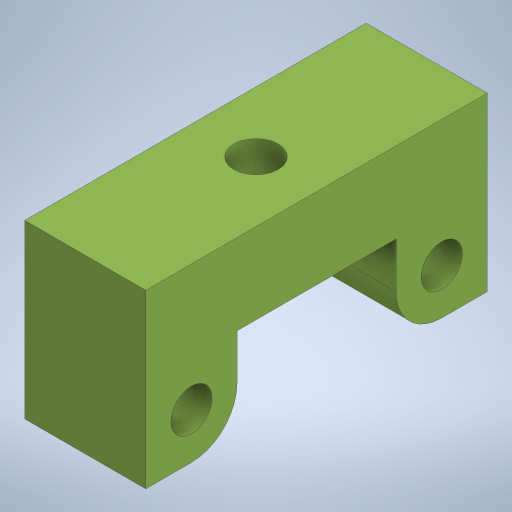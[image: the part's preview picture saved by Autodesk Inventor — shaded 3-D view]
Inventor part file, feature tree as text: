
AUTODESK INVENTOR PART (.ipt)
format: ipt  version: 2023.2 (Build 272271030, 271C)  size: 252,416 bytes
history: native  units: mm
features: extrude x3, sketch x2, plane x1, projected_geometry x1
ambient origin geometry x8: Origin, YZ Plane, XZ Plane, XY Plane, X Axis, Y Axis, Z Axis, Center Point
bodies: Body1 (feature_tree)
feature tree (7):
  sketch  "Sketch3"  dims[d19=11.3mm d20=5.65mm d23=10.0mm]
  plane  "Work Plane1"
  extrude  "Extrusion5"  Depth=10.0mm
  sketch  "Sketch5"  dims[d24=10.0mm d25=11.3mm d26=5.1mm d29=5.5mm d36=21.15mm d37=15.0mm d38=0.0mm d40=8.1mm d41=5.5mm d42=0.0mm d43=0.0mm d44=3.1mm d45=0.0mm d3=0.5mm d4=0.872665mm d5=0.5mm d6=0.872665mm]
  extrude  "Extrusion6"  Depth=11.3mm
  extrude  "Extrusion7"  Depth=15.0mm
  projected_geometry  "Projected Loop2"
